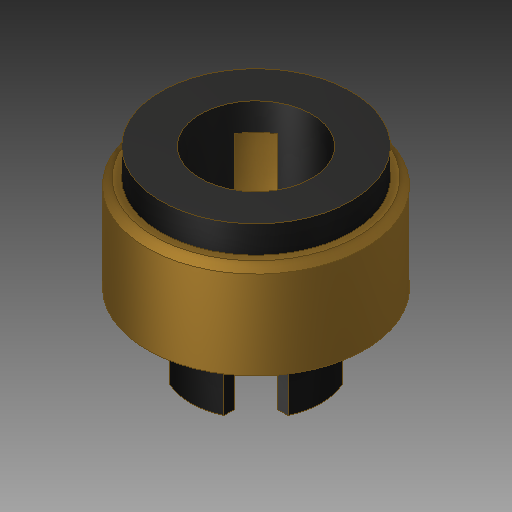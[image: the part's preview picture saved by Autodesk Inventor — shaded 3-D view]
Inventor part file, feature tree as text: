
AUTODESK INVENTOR PART (.ipt)
format: ipt  version: 2019 (Build 230136000, 136)  size: 172,544 bytes
history: native  units: mm
features: other x6, sketch x3
ambient origin geometry x8: Origin, YZ Plane, XZ Plane, XY Plane, X Axis, Y Axis, Z Axis, Center Point
bodies: Solid1 (feature_tree)
feature tree (9):
  other  "Collet.ipt"
  other  "Solid1::Collet.ipt"
  other  "TaggingFeature1"
  sketch  "Sketch1"  dims[d0=10.0mm]
  sketch  "Sketch2"
  sketch  "Sketch3"
  other  "Work Axis1"
  other  "Work Axis2"
  other  "Work Axis3"
